# Revit family: Haworth_BuzziPicNic_RoundCollaborativeTable
name_source: partatom
category: Furniture
revit_build: Autodesk Revit 2018 (Build: 20170223_1515(x64)
units: mm (PartAtom-declared; Revit-internal decimal feet)

## family parameters
Always vertical = Yes
Cut with Voids When Loaded = No
OmniClass Number = 23.40.20.00
OmniClass Title = General Furniture and Specialties
Room Calculation Point = No
Shared = No
Work Plane-Based = No

## types (2) — shared parameters
Assembly Code = E2020200
Glide Finish = Haworth _ Polymer _ Black
Manufacturer = Haworth
Model = HCBZ-PNTR
Revision = 1
Size = Verify Final Dim. w/ Haworth
URL = http://www.haworth.com
URL - Product = https://www.haworth.com
Warranty = http://www.haworth.com
zero-valued in all types: Actual Depth, Actual Height, Actual Width, Inner Void Radius, Outer Void Radius, Radius, Top Inner Radius

## per-type parameters (varying)
| type | Description | Large | Small |
| HCBZ-PNTR-SSW | Haworth BuzziPicNic Small Round Table | No | Yes |
| HCBZ-PNTR-LSW | Haworth BuzziPicNic Large Round Table | Yes | No |

## geometry (parser evidence)
native form markers: Sweep x3
no freeform markers — native parametric forms only
